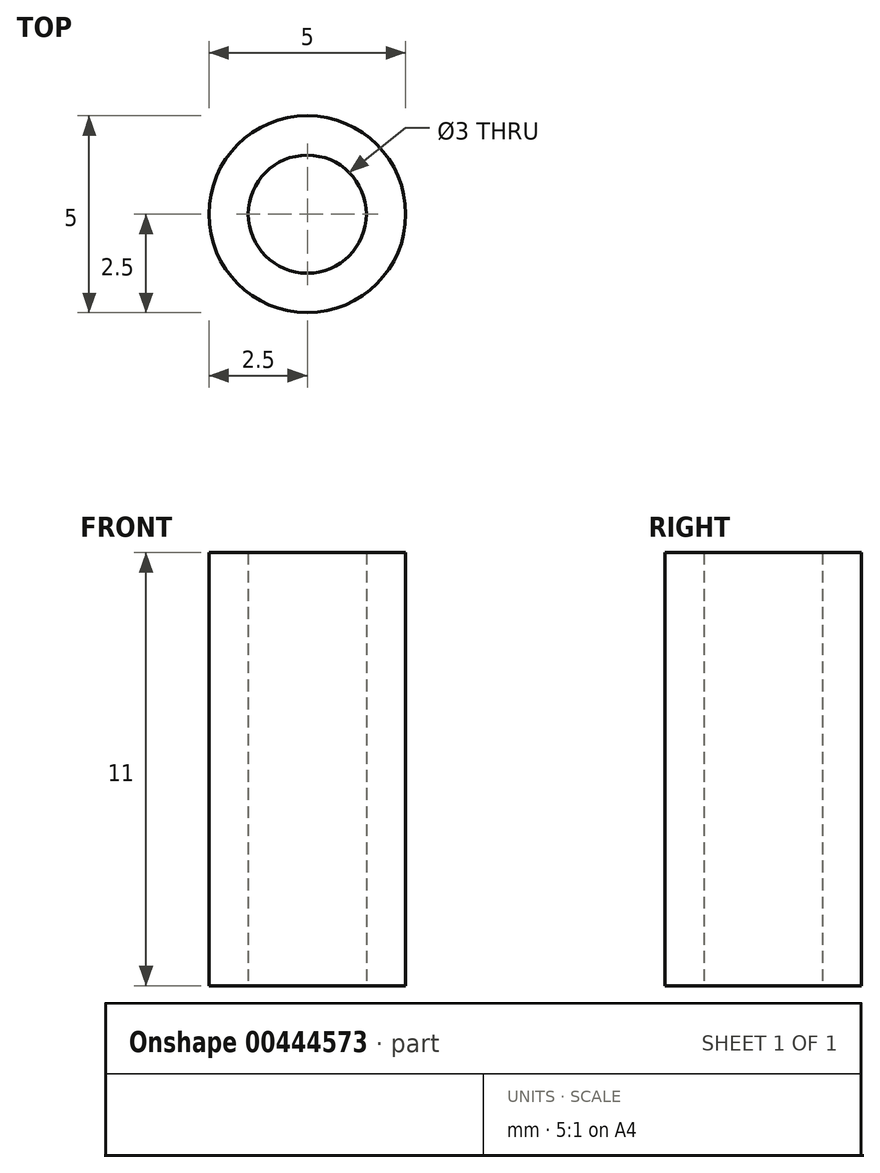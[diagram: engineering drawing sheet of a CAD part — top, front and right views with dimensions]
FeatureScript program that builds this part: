
annotation { "Feature Type Name" : "Feature", "Feature Type Description" : "" }
export const myFeature = defineFeature(function(context is Context, id is Id, definition is map)
    precondition{}
    {
        {
            var Q0;
            Q0=qCreatedBy(makeId("Top.planeOp"),FACE);
            var sketch = newSketch(context, id + "F0", { "sketchPlane" : qUnion([Q0])});
            skCircle(sketch, "E0", {"center": v(0, 0) * mm, "radius": 1.5 * mm});
            skCircle(sketch, "E1", {"center": v(0, 0) * mm, "radius": 2.5 * mm});
            skSolve(sketch);
        }
        {
            var Q0;
            Q0 = qSketchRegion(id + "F0", true);
            extrude(context, id + "F1", {"entities" : qUnion([Q0]), "depth" : 11 * mm});
        }
    });
